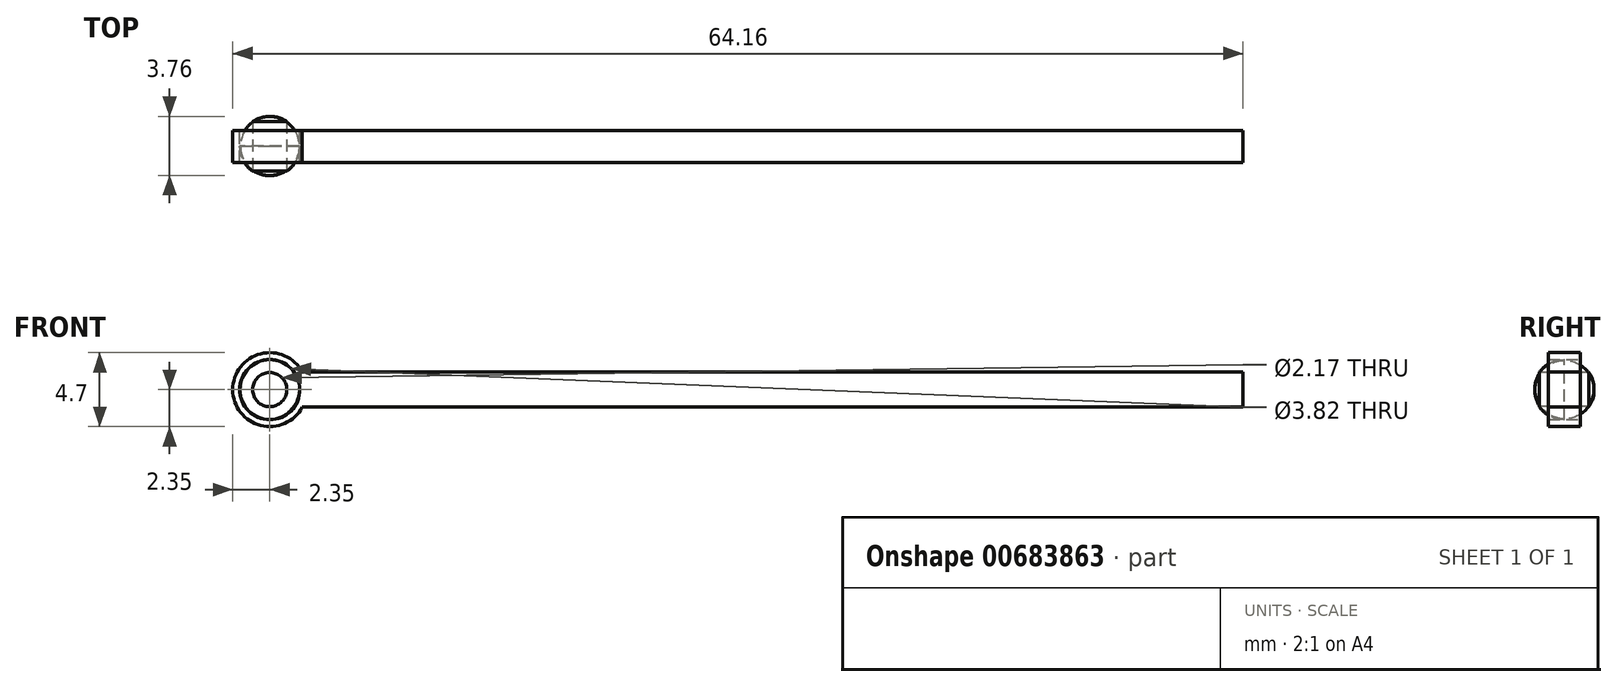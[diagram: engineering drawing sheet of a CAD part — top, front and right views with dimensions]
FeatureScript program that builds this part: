
annotation { "Feature Type Name" : "Feature", "Feature Type Description" : "" }
export const myFeature = defineFeature(function(context is Context, id is Id, definition is map)
    precondition{}
    {
        {
            var Q0;
            Q0=qCreatedBy(makeId("Front.planeOp"),FACE);
            var sketch = newSketch(context, id + "F0", { "sketchPlane" : qUnion([Q0])});
            skCircle(sketch, "E0", {"center": v(0, 0) * mm, "radius": 1.9 * mm});
            skSolve(sketch);
        }
        {
            var Q0;
            Q0=makeQuery(id+"F0.imprint","IMPRINT",FACE,{"disambiguationData":[TD([[makeQuery(id+"F0.imprint","IMPRINT",EDGE,{"derivedFrom":sQuery(id+"F0.wireOp",EDGE,"E0")}),1.0]])]});
            extrude(context, id + "F1", {"entities" : qUnion([Q0]), "depth" : 1.9 * mm, "offsetDistance" : 25.4 * mm, "hasSecondDirection" : true, "secondDirectionOppositeDirection" : true, "secondDirectionDepth" : 1.9 * mm});
        }
        {
            var Q0;
            Q0=makeQuery(id+"F1.opExtrude","CAP_EDGE",EDGE,{"disambiguationData":[OSD([sQuery(id+"F0.wireOp",EDGE,"E0")])],"isStart":false});
            var Q1;
            Q1=makeQuery(id+"F1.opExtrude","CAP_EDGE",EDGE,{"disambiguationData":[OSD([sQuery(id+"F0.wireOp",EDGE,"E0")])],"isStart":true});
            fillet(context, id + "F2", {"entities" : qUnion([Q0, Q1]), "radius" : 1.88 * mm, "tangentPropagation" : true, "allowEdgeOverflow" : false});
        }
        {
            var Q0;
            Q0=qCreatedBy(makeId("Front.planeOp"),FACE);
            var sketch = newSketch(context, id + "F3", { "sketchPlane" : qUnion([Q0])});
            skCircle(sketch, "E1", {"center": v(0, 0) * mm, "radius": 1.08 * mm});
            skSolve(sketch);
        }
        {
            var Q0;
            Q0 = qSketchRegion(id + "F3", true);
            extrude(context, id + "F4", {"entities" : qUnion([Q0]), "operationType" : NewBodyOperationType.REMOVE, "oppositeDirection" : true, "depth" : 1.9 * mm, "offsetDistance" : 25.4 * mm, "hasSecondDirection" : true, "secondDirectionOppositeDirection" : false, "secondDirectionDepth" : 1.9 * mm});
        }
        {
            var Q0;
            Q0=qCreatedBy(makeId("Front.planeOp"),FACE);
            var sketch = newSketch(context, id + "F5", { "sketchPlane" : qUnion([Q0])});
            skCircle(sketch, "E2", {"center": v(0, 0) * mm, "radius": 1.9 * mm});
            skCircle(sketch, "E3", {"center": v(0, 0) * mm, "radius": 2.35 * mm});
            skSolve(sketch);
        }
        {
            var Q0;
            Q0=makeQuery(id+"F5.imprint","IMPRINT",FACE,{"disambiguationData":[TD([[makeQuery(id+"F5.imprint","IMPRINT",EDGE,{"derivedFrom":sQuery(id+"F5.wireOp",EDGE,"E2")}),-1.0]])]});
            extrude(context, id + "F6", {"entities" : qUnion([Q0]), "depth" : 1.02 * mm, "offsetDistance" : 25.4 * mm, "hasSecondDirection" : true, "secondDirectionOppositeDirection" : true, "secondDirectionDepth" : 1.02 * mm});
        }
        {
            var Q0;
            Q0=makeQuery(id+"F6.opExtrude","CAP_FACE",FACE,{"disambiguationData":[OSD([sQuery(id+"F5.wireOp",EDGE,"E2"),sQuery(id+"F5.wireOp",EDGE,"E3")])],"isStart":false});
            var sketch = newSketch(context, id + "F7", { "sketchPlane" : qUnion([Q0])});
            skLineSegment(sketch, "E4.bottom", {"start": v(5.93, -1.11) * mm, "end": v(2.01, -1.11) * mm});
            skLineSegment(sketch, "E4.top", {"start": v(5.93, 1.11) * mm, "end": v(2.01, 1.11) * mm});
            skLineSegment(sketch, "E4.left", {"start": v(5.93, -1.11) * mm, "end": v(5.93, 1.11) * mm});
            skLineSegment(sketch, "E4.right", {"start": v(2.01, -1.11) * mm, "end": v(2.01, 1.11) * mm});
            skPoint(sketch, "E4.middle", {"position": v(3.97, 0) * mm});
            skSolve(sketch);
        }
        {
            var Q0;
            {var subQ0=sQuery(id+"F7.wireOp",EDGE,"E4.left");Q0=makeQuery(id+"F7.imprint","IMPRINT",FACE,{"disambiguationData":[TD([[makeQuery(id+"F7.imprint","IMPRINT",EDGE,{"derivedFrom":subQ0}),1.0]])]});}
            var Q1;
            {var subQ0=sQuery(id+"F7.wireOp",EDGE,"E4.right");Q1=makeQuery(id+"F7.imprint","IMPRINT",FACE,{"disambiguationData":[TD([[makeQuery(id+"F7.imprint","IMPRINT",EDGE,{"derivedFrom":subQ0}),-1.0]])]});}
            extrude(context, id + "F8", {"entities" : qUnion([Q0, Q1]), "operationType" : NewBodyOperationType.ADD, "oppositeDirection" : true, "depth" : 2.03 * mm, "offsetDistance" : 25.4 * mm});
        }
        {
            var Q0;
            Q0=makeQuery(id+"F8.opExtrude","SWEPT_FACE",FACE,{"disambiguationData":[OSD([sQuery(id+"F7.wireOp",EDGE,"E4.left")])]});
            var sketch = newSketch(context, id + "F9", { "sketchPlane" : qUnion([Q0])});
            skLineSegment(sketch, "E5.bottom", {"start": v(-1.02, 1.11) * mm, "end": v(1.02, 1.11) * mm});
            skLineSegment(sketch, "E5.top", {"start": v(-1.02, -1.11) * mm, "end": v(1.02, -1.11) * mm});
            skLineSegment(sketch, "E5.left", {"start": v(-1.02, 1.11) * mm, "end": v(-1.02, -1.11) * mm});
            skLineSegment(sketch, "E5.right", {"start": v(1.02, 1.11) * mm, "end": v(1.02, -1.11) * mm});
            skSolve(sketch);
        }
        {
            var Q0;
            Q0 = qSketchRegion(id + "F9", true);
            extrude(context, id + "F10", {"entities" : qUnion([Q0]), "operationType" : NewBodyOperationType.ADD, "depth" : 55.88 * mm, "offsetDistance" : 25.4 * mm});
        }
    });
